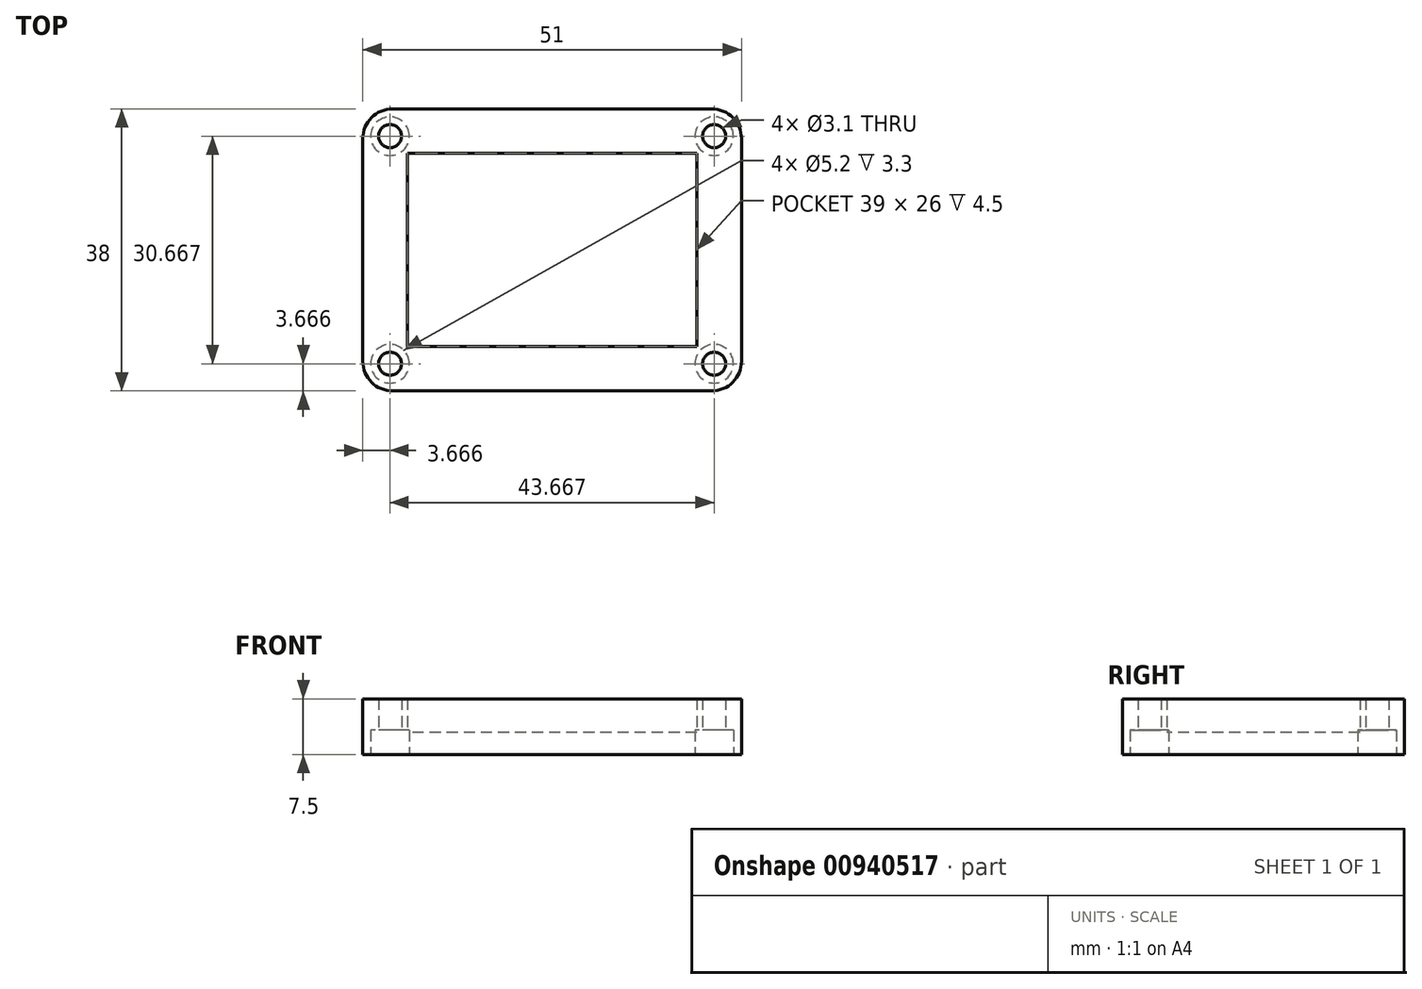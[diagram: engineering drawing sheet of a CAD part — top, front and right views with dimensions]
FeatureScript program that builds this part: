
annotation { "Feature Type Name" : "Feature", "Feature Type Description" : "" }
export const myFeature = defineFeature(function(context is Context, id is Id, definition is map)
    precondition{}
    {
        {
            var Q0;
            Q0=qCreatedBy(makeId("Top.planeOp"),FACE);
            var sketch = newSketch(context, id + "F0", { "sketchPlane" : qUnion([Q0])});
            skLineSegment(sketch, "E0.bottom", {"start": v(21.5, 19) * mm, "end": v(-21.5, 19) * mm});
            skLineSegment(sketch, "E0.top", {"start": v(21.5, -19) * mm, "end": v(-21.5, -19) * mm});
            skLineSegment(sketch, "E0.left", {"start": v(25.5, 15) * mm, "end": v(25.5, -15) * mm});
            skLineSegment(sketch, "E0.right", {"start": v(-25.5, 15) * mm, "end": v(-25.5, -15) * mm});
            skPoint(sketch, "E0.middle", {"position": v(0, 0) * mm});
            skLineSegment(sketch, "E1.bottom", {"start": v(19.5, 13) * mm, "end": v(-19.5, 13) * mm});
            skLineSegment(sketch, "E1.top", {"start": v(19.5, -13) * mm, "end": v(-19.5, -13) * mm});
            skLineSegment(sketch, "E1.left", {"start": v(19.5, 13) * mm, "end": v(19.5, -13) * mm});
            skLineSegment(sketch, "E1.right", {"start": v(-19.5, 13) * mm, "end": v(-19.5, -13) * mm});
            skLineSegment(sketch, "E2", {"start": v(19.5, 0) * mm, "end": v(25.5, 0) * mm, "construction": true});
            skLineSegment(sketch, "E3.bottom", {"start": v(25.5, 7) * mm, "end": v(19.5, 7) * mm});
            skLineSegment(sketch, "E3.top", {"start": v(25.5, -7) * mm, "end": v(19.5, -7) * mm});
            skLineSegment(sketch, "E3.left", {"start": v(25.5, 7) * mm, "end": v(25.5, -7) * mm});
            skLineSegment(sketch, "E3.right", {"start": v(19.5, 7) * mm, "end": v(19.5, -7) * mm});
            skPoint(sketch, "E3.middle", {"position": v(22.5, 0) * mm});
            skLineSegment(sketch, "E4", {"start": v(25.1, 7) * mm, "end": v(25.1, -7) * mm});
            skLineSegment(sketch, "E5.bottom", {"start": v(25.5, 4.25) * mm, "end": v(19.5, 4.25) * mm});
            skLineSegment(sketch, "E5.top", {"start": v(25.5, -4.25) * mm, "end": v(19.5, -4.25) * mm});
            skLineSegment(sketch, "E5.left", {"start": v(25.5, 4.25) * mm, "end": v(25.5, -4.25) * mm});
            skLineSegment(sketch, "E5.right", {"start": v(19.5, 4.25) * mm, "end": v(19.5, -4.25) * mm});
            skLineSegment(sketch, "E6", {"start": v(9.5, 19) * mm, "end": v(9.5, 13) * mm});
            skLineSegment(sketch, "E7", {"start": v(-3.7, 19) * mm, "end": v(-3.7, 13) * mm});
            skLineSegment(sketch, "E8", {"start": v(-5.7, 19) * mm, "end": v(-5.7, 13) * mm});
            skLineSegment(sketch, "E9", {"start": v(-18.9, 19) * mm, "end": v(-18.9, 13) * mm});
            skLineSegment(sketch, "E10.MirrorCS", {"start": v(-18.9, -19) * mm, "end": v(-18.9, -13) * mm});
            skLineSegment(sketch, "E11.MirrorCS", {"start": v(-5.7, -19) * mm, "end": v(-5.7, -13) * mm});
            skLineSegment(sketch, "E12.MirrorCS", {"start": v(-3.7, -19) * mm, "end": v(-3.7, -13) * mm});
            skLineSegment(sketch, "E13.MirrorCS", {"start": v(9.5, -19) * mm, "end": v(9.5, -13) * mm});
            skPoint(sketch, "E14.visualSharp", {"position": v(-25.5, 19) * mm});
            skArc(sketch, "E14.filletArc", {"start": v(-21.5, 19) * mm, "mid": v(-24.33, 17.83) * mm, "end": v(-25.5, 15) * mm});
            skPoint(sketch, "E15.visualSharp", {"position": v(-25.5, -19) * mm});
            skArc(sketch, "E15.filletArc", {"start": v(-25.5, -15) * mm, "mid": v(-24.33, -17.83) * mm, "end": v(-21.5, -19) * mm});
            skPoint(sketch, "E16.visualSharp", {"position": v(25.5, -19) * mm});
            skArc(sketch, "E16.filletArc", {"start": v(21.5, -19) * mm, "mid": v(24.33, -17.83) * mm, "end": v(25.5, -15) * mm});
            skPoint(sketch, "E17.visualSharp", {"position": v(25.5, 19) * mm});
            skArc(sketch, "E17.filletArc", {"start": v(25.5, 15) * mm, "mid": v(24.33, 17.83) * mm, "end": v(21.5, 19) * mm});
            skLineSegment(sketch, "E18", {"start": v(19.5, 13) * mm, "end": v(25.5, 19) * mm, "construction": true});
            skCircle(sketch, "E19", {"center": v(21.83, 15.33) * mm, "radius": 2.6 * mm});
            skCircle(sketch, "E20", {"center": v(21.83, 15.33) * mm, "radius": 1.38 * mm});
            skCircle(sketch, "E21", {"center": v(21.83, 15.33) * mm, "radius": 1.55 * mm});
            skCircle(sketch, "E22.0.1.0", {"center": v(21.83, -15.33) * mm, "radius": 2.6 * mm});
            skCircle(sketch, "E22.0.1.1", {"center": v(21.83, -15.33) * mm, "radius": 1.55 * mm});
            skCircle(sketch, "E22.0.1.2", {"center": v(21.83, -15.33) * mm, "radius": 1.38 * mm});
            skCircle(sketch, "E22.1.0.0", {"center": v(-21.83, 15.33) * mm, "radius": 2.6 * mm});
            skCircle(sketch, "E22.1.0.1", {"center": v(-21.83, 15.33) * mm, "radius": 1.55 * mm});
            skCircle(sketch, "E22.1.0.2", {"center": v(-21.83, 15.33) * mm, "radius": 1.38 * mm});
            skCircle(sketch, "E22.1.1.0", {"center": v(-21.83, -15.33) * mm, "radius": 2.6 * mm});
            skCircle(sketch, "E22.1.1.1", {"center": v(-21.83, -15.33) * mm, "radius": 1.55 * mm});
            skCircle(sketch, "E22.1.1.2", {"center": v(-21.83, -15.33) * mm, "radius": 1.38 * mm});
            skLineSegment(sketch, "E22.direction1", {"start": v(21.83, 15.33) * mm, "end": v(-21.83, 15.33) * mm, "construction": true});
            skLineSegment(sketch, "E22.direction2", {"start": v(21.83, 15.33) * mm, "end": v(21.83, -15.33) * mm, "construction": true});
            skLineSegment(sketch, "E23", {"start": v(-19.5, 13) * mm, "end": v(-25.5, 19) * mm, "construction": true});
            skLineSegment(sketch, "E24", {"start": v(19.5, -13) * mm, "end": v(25.5, -19) * mm, "construction": true});
            skSolve(sketch);
        }
        {
            var Q0;
            {var subQ0=sQuery(id+"F0.wireOp",EDGE,"E1.right");Q0=makeQuery(id+"F0.imprint","IMPRINT",FACE,{"disambiguationData":[TD([[makeQuery(id+"F0.imprint","IMPRINT",EDGE,{"derivedFrom":subQ0}),1.0]])]});}
            extrude(context, id + "F1", {"entities" : qUnion([Q0]), "depth" : 3 * mm, "offsetDistance" : 25 * mm});
        }
        {
            var Q0;
            Q0=makeQuery(id+"F0.imprint","IMPRINT",FACE,{"disambiguationData":[TD([[makeQuery(id+"F0.imprint","IMPRINT",EDGE,{"derivedFrom":sQuery(id+"F0.wireOp",EDGE,"E0.right")}),1.0]])]});
            var Q1;
            {var subQ2=sQuery(id+"F0.wireOp",EDGE,"E10.MirrorCS");Q1=makeQuery(id+"F0.imprint","IMPRINT",FACE,{"disambiguationData":[TD([[makeQuery(id+"F0.imprint","IMPRINT",EDGE,{"derivedFrom":subQ2}),-1.0]])]});}
            var Q2;
            {var subQ0=sQuery(id+"F0.wireOp",EDGE,"E11.MirrorCS");Q2=makeQuery(id+"F0.imprint","IMPRINT",FACE,{"disambiguationData":[TD([[makeQuery(id+"F0.imprint","IMPRINT",EDGE,{"derivedFrom":subQ0}),-1.0]])]});}
            var Q3;
            {var subQ0=sQuery(id+"F0.wireOp",EDGE,"E12.MirrorCS");Q3=makeQuery(id+"F0.imprint","IMPRINT",FACE,{"disambiguationData":[TD([[makeQuery(id+"F0.imprint","IMPRINT",EDGE,{"derivedFrom":subQ0}),-1.0]])]});}
            var Q4;
            {var subQ5=sQuery(id+"F0.wireOp",EDGE,"E13.MirrorCS");Q4=makeQuery(id+"F0.imprint","IMPRINT",FACE,{"disambiguationData":[TD([[makeQuery(id+"F0.imprint","IMPRINT",EDGE,{"derivedFrom":subQ5}),-1.0]])]});}
            var Q5;
            {var subQ0=sQuery(id+"F0.wireOp",EDGE,"E5.bottom");var subQ1=sQuery(id+"F0.wireOp",EDGE,"E1.left");var subQ2=makeQuery(id+"F0.imprint","INTERSECT",VERTEX,{"derivedFrom":[subQ1,subQ0]});Q5=makeQuery(id+"F0.imprint","IMPRINT",FACE,{"disambiguationData":[TD([[makeQuery(id+"F0.imprint","IMPRINT",EDGE,{"disambiguationData":[TD([[subQ2,-1.0]])],"derivedFrom":subQ1}),1.0]])]});}
            var Q6;
            {var subQ0=sQuery(id+"F0.wireOp",EDGE,"E3.top");var subQ1=sQuery(id+"F0.wireOp",EDGE,"E0.left");var subQ2=makeQuery(id+"F0.imprint","INTERSECT",VERTEX,{"derivedFrom":[subQ1,subQ0]});Q6=makeQuery(id+"F0.imprint","IMPRINT",FACE,{"disambiguationData":[TD([[makeQuery(id+"F0.imprint","IMPRINT",EDGE,{"disambiguationData":[TD([[subQ2,1.0]])],"derivedFrom":subQ1}),-1.0]])]});}
            var Q7;
            {var subQ0=sQuery(id+"F0.wireOp",EDGE,"E5.top");var subQ1=sQuery(id+"F0.wireOp",EDGE,"E1.left");var subQ2=makeQuery(id+"F0.imprint","INTERSECT",VERTEX,{"derivedFrom":[subQ1,subQ0]});Q7=makeQuery(id+"F0.imprint","IMPRINT",FACE,{"disambiguationData":[TD([[makeQuery(id+"F0.imprint","IMPRINT",EDGE,{"disambiguationData":[TD([[subQ2,-1.0]])],"derivedFrom":subQ1}),1.0]])]});}
            var Q8;
            {var subQ0=sQuery(id+"F0.wireOp",EDGE,"E5.bottom");var subQ1=sQuery(id+"F0.wireOp",EDGE,"E0.left");var subQ2=makeQuery(id+"F0.imprint","INTERSECT",VERTEX,{"derivedFrom":[subQ1,subQ0]});Q8=makeQuery(id+"F0.imprint","IMPRINT",FACE,{"disambiguationData":[TD([[makeQuery(id+"F0.imprint","IMPRINT",EDGE,{"disambiguationData":[TD([[subQ2,-1.0]])],"derivedFrom":subQ1}),-1.0]])]});}
            var Q9;
            {var subQ0=sQuery(id+"F0.wireOp",EDGE,"E5.bottom");var subQ1=sQuery(id+"F0.wireOp",EDGE,"E1.left");var subQ2=makeQuery(id+"F0.imprint","INTERSECT",VERTEX,{"derivedFrom":[subQ1,subQ0]});Q9=makeQuery(id+"F0.imprint","IMPRINT",FACE,{"disambiguationData":[TD([[makeQuery(id+"F0.imprint","IMPRINT",EDGE,{"disambiguationData":[TD([[subQ2,1.0]])],"derivedFrom":subQ1}),1.0]])]});}
            var Q10;
            {var subQ0=sQuery(id+"F0.wireOp",EDGE,"E5.bottom");var subQ1=sQuery(id+"F0.wireOp",EDGE,"E0.left");var subQ2=makeQuery(id+"F0.imprint","INTERSECT",VERTEX,{"derivedFrom":[subQ1,subQ0]});Q10=makeQuery(id+"F0.imprint","IMPRINT",FACE,{"disambiguationData":[TD([[makeQuery(id+"F0.imprint","IMPRINT",EDGE,{"disambiguationData":[TD([[subQ2,1.0]])],"derivedFrom":subQ1}),-1.0]])]});}
            var Q11;
            {var subQ0=sQuery(id+"F0.wireOp",EDGE,"E6");Q11=makeQuery(id+"F0.imprint","IMPRINT",FACE,{"disambiguationData":[TD([[makeQuery(id+"F0.imprint","IMPRINT",EDGE,{"derivedFrom":subQ0}),1.0]])]});}
            var Q12;
            {var subQ0=sQuery(id+"F0.wireOp",EDGE,"E6");Q12=makeQuery(id+"F0.imprint","IMPRINT",FACE,{"disambiguationData":[TD([[makeQuery(id+"F0.imprint","IMPRINT",EDGE,{"derivedFrom":subQ0}),-1.0]])]});}
            var Q13;
            {var subQ2=sQuery(id+"F0.wireOp",EDGE,"E7");Q13=makeQuery(id+"F0.imprint","IMPRINT",FACE,{"disambiguationData":[TD([[makeQuery(id+"F0.imprint","IMPRINT",EDGE,{"derivedFrom":subQ2}),-1.0]])]});}
            var Q14;
            {var subQ0=sQuery(id+"F0.wireOp",EDGE,"E8");Q14=makeQuery(id+"F0.imprint","IMPRINT",FACE,{"disambiguationData":[TD([[makeQuery(id+"F0.imprint","IMPRINT",EDGE,{"derivedFrom":subQ0}),-1.0]])]});}
            var Q15;
            Q15=makeQuery(id+"F0.imprint","IMPRINT",FACE,{"disambiguationData":[TD([[makeQuery(id+"F0.imprint","IMPRINT",EDGE,{"derivedFrom":sQuery(id+"F0.wireOp",EDGE,"E22.1.0.0")}),1.0]])]});
            var Q16;
            Q16=makeQuery(id+"F0.imprint","IMPRINT",FACE,{"disambiguationData":[TD([[makeQuery(id+"F0.imprint","IMPRINT",EDGE,{"derivedFrom":sQuery(id+"F0.wireOp",EDGE,"E22.1.1.0")}),1.0]])]});
            var Q17;
            Q17=makeQuery(id+"F0.imprint","IMPRINT",FACE,{"disambiguationData":[TD([[makeQuery(id+"F0.imprint","IMPRINT",EDGE,{"derivedFrom":sQuery(id+"F0.wireOp",EDGE,"E22.0.1.0")}),1.0]])]});
            var Q18;
            Q18=makeQuery(id+"F0.imprint","IMPRINT",FACE,{"disambiguationData":[TD([[makeQuery(id+"F0.imprint","IMPRINT",EDGE,{"derivedFrom":sQuery(id+"F0.wireOp",EDGE,"E19")}),1.0]])]});
            extrude(context, id + "F2", {"entities" : qUnion([Q0, Q1, Q2, Q3, Q4, Q5, Q6, Q7, Q8, Q9, Q10, Q11, Q12, Q13, Q14, Q15, Q16, Q17, Q18]), "operationType" : NewBodyOperationType.ADD, "depth" : (3 + 4.5) * mm, "offsetDistance" : 25 * mm});
        }
        {
            var Q0;
            Q0=makeQuery(id+"F0.imprint","IMPRINT",FACE,{"disambiguationData":[TD([[makeQuery(id+"F0.imprint","IMPRINT",EDGE,{"derivedFrom":sQuery(id+"F0.wireOp",EDGE,"E22.1.1.0")}),1.0]])]});
            var Q1;
            Q1=makeQuery(id+"F0.imprint","IMPRINT",FACE,{"disambiguationData":[TD([[makeQuery(id+"F0.imprint","IMPRINT",EDGE,{"derivedFrom":sQuery(id+"F0.wireOp",EDGE,"E22.0.1.0")}),1.0]])]});
            var Q2;
            Q2=makeQuery(id+"F0.imprint","IMPRINT",FACE,{"disambiguationData":[TD([[makeQuery(id+"F0.imprint","IMPRINT",EDGE,{"derivedFrom":sQuery(id+"F0.wireOp",EDGE,"E19")}),1.0]])]});
            var Q3;
            Q3=makeQuery(id+"F0.imprint","IMPRINT",FACE,{"disambiguationData":[TD([[makeQuery(id+"F0.imprint","IMPRINT",EDGE,{"derivedFrom":sQuery(id+"F0.wireOp",EDGE,"E22.1.0.0")}),1.0]])]});
            extrude(context, id + "F3", {"entities" : qUnion([Q0, Q1, Q2, Q3]), "operationType" : NewBodyOperationType.REMOVE, "depth" : 3.3 * mm, "offsetDistance" : 25 * mm});
        }
    });
